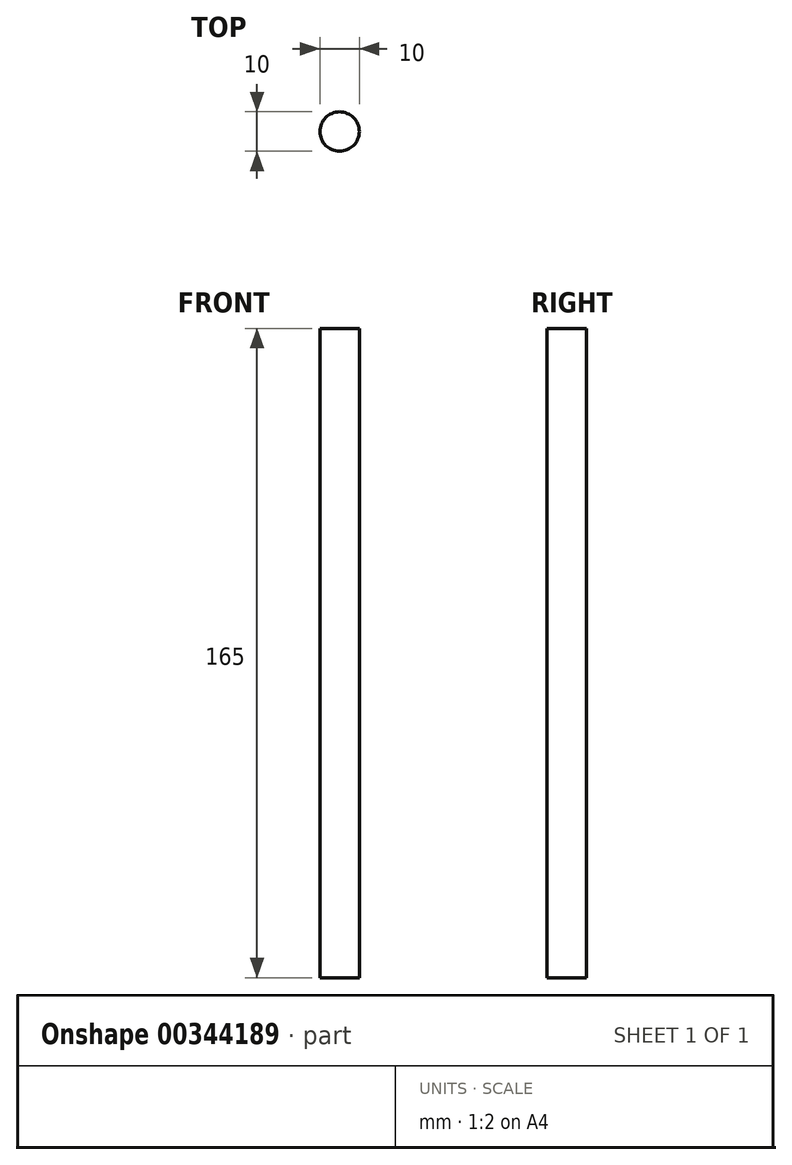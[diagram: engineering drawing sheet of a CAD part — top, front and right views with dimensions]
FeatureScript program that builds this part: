
annotation { "Feature Type Name" : "Feature", "Feature Type Description" : "" }
export const myFeature = defineFeature(function(context is Context, id is Id, definition is map)
    precondition{}
    {
        {
            var Q0;
            Q0=qCreatedBy(makeId("Top.planeOp"),FACE);
            var sketch = newSketch(context, id + "F0", { "sketchPlane" : qUnion([Q0])});
            skCircle(sketch, "E0", {"center": v(0, 0) * mm, "radius": 5 * mm});
            skSolve(sketch);
        }
        {
            var Q0;
            Q0 = qSketchRegion(id + "F0", true);
            extrude(context, id + "F1", {"entities" : qUnion([Q0]), "depth" : 165 * mm});
        }
    });
